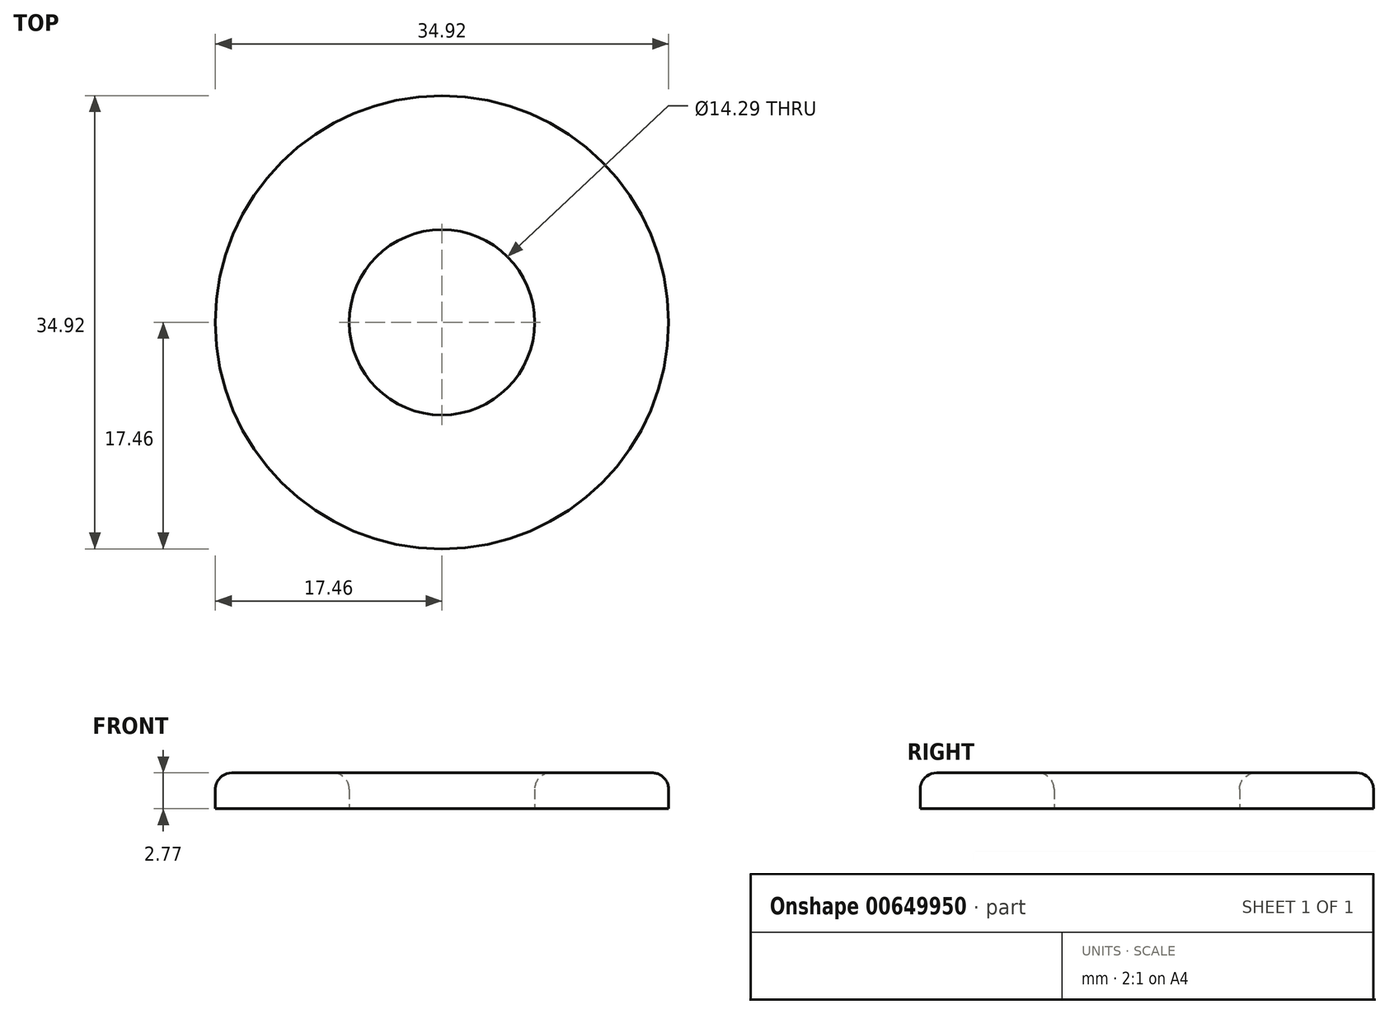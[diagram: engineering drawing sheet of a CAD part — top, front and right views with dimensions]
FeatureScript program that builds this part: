
annotation { "Feature Type Name" : "Feature", "Feature Type Description" : "" }
export const myFeature = defineFeature(function(context is Context, id is Id, definition is map)
    precondition{}
    {
        {
            var Q0;
            Q0=qCreatedBy(makeId("Top.planeOp"),FACE);
            var sketch = newSketch(context, id + "F0", { "sketchPlane" : qUnion([Q0])});
            skCircle(sketch, "E0", {"center": v(0, 0) * mm, "radius": 7.14 * mm});
            skCircle(sketch, "E1", {"center": v(0, 0) * mm, "radius": 17.46 * mm});
            skSolve(sketch);
        }
        {
            var Q0;
            Q0=makeQuery(id+"F0.imprint","IMPRINT",FACE,{"disambiguationData":[TD([[makeQuery(id+"F0.imprint","IMPRINT",EDGE,{"derivedFrom":sQuery(id+"F0.wireOp",EDGE,"E0")}),-1.0]])]});
            extrude(context, id + "F1", {"entities" : qUnion([Q0]), "depth" : 2.77 * mm, "offsetDistance" : 25.4 * mm});
        }
        {
            var Q0;
            Q0=makeQuery(id+"F1.opExtrude","CAP_EDGE",EDGE,{"disambiguationData":[OSD([sQuery(id+"F0.wireOp",EDGE,"E1")])],"isStart":false});
            var Q1;
            Q1=makeQuery(id+"F1.opExtrude","CAP_EDGE",EDGE,{"disambiguationData":[OSD([sQuery(id+"F0.wireOp",EDGE,"E0")])],"isStart":false});
            fillet(context, id + "F2", {"entities" : qUnion([Q0, Q1]), "radius" : 1.27 * mm, "tangentPropagation" : true, "allowEdgeOverflow" : false});
        }
    });
